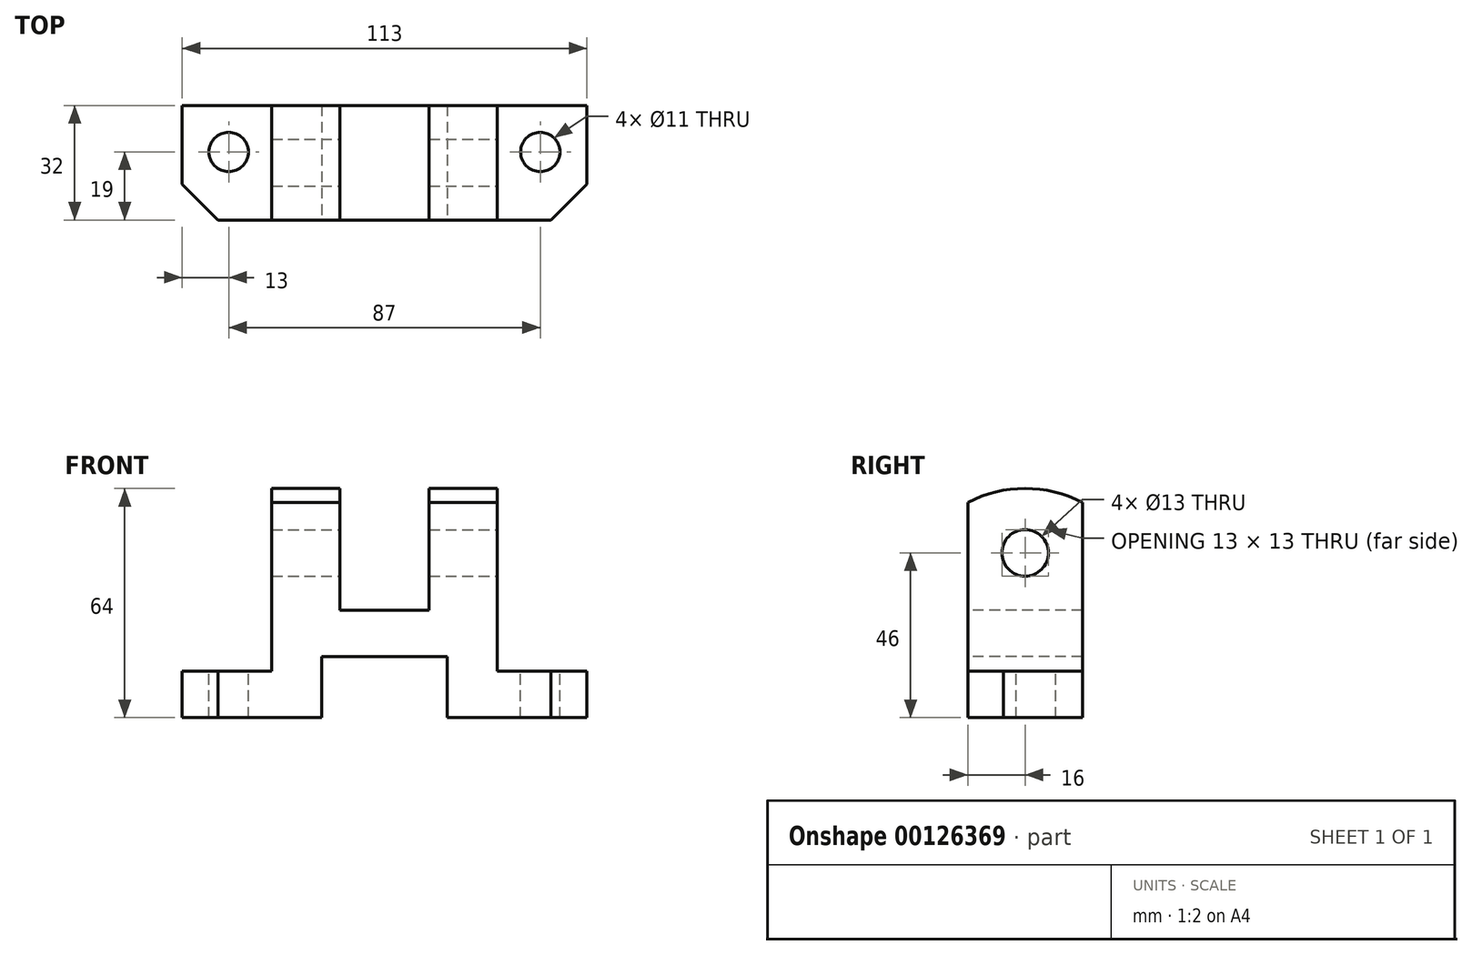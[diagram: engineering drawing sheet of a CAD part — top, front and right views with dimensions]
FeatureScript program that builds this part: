
annotation { "Feature Type Name" : "Feature", "Feature Type Description" : "" }
export const myFeature = defineFeature(function(context is Context, id is Id, definition is map)
    precondition{}
    {
        {
            var Q0;
            Q0=qCreatedBy(makeId("Front.planeOp"),FACE);
            var sketch = newSketch(context, id + "F0", { "sketchPlane" : qUnion([Q0])});
            skLineSegment(sketch, "E0", {"start": v(0, 0) * mm, "end": v(0, 13) * mm});
            skLineSegment(sketch, "E1", {"start": v(0, 13) * mm, "end": v(25, 13) * mm});
            skLineSegment(sketch, "E2", {"start": v(25, 13) * mm, "end": v(25, 64) * mm});
            skLineSegment(sketch, "E3", {"start": v(25, 64) * mm, "end": v(44, 64) * mm});
            skLineSegment(sketch, "E4", {"start": v(44, 64) * mm, "end": v(44, 30) * mm});
            skLineSegment(sketch, "E5", {"start": v(44, 30) * mm, "end": v(69, 30) * mm});
            skLineSegment(sketch, "E6", {"start": v(69, 30) * mm, "end": v(69, 64) * mm});
            skLineSegment(sketch, "E7", {"start": v(69, 64) * mm, "end": v(88, 64) * mm});
            skLineSegment(sketch, "E8", {"start": v(88, 64) * mm, "end": v(88, 13) * mm});
            skLineSegment(sketch, "E9", {"start": v(88, 13) * mm, "end": v(113, 13) * mm});
            skLineSegment(sketch, "E10", {"start": v(113, 13) * mm, "end": v(113, 0) * mm});
            skLineSegment(sketch, "E11", {"start": v(113, 0) * mm, "end": v(74, 0) * mm});
            skLineSegment(sketch, "E12", {"start": v(74, 0) * mm, "end": v(74, 17) * mm});
            skLineSegment(sketch, "E13", {"start": v(74, 17) * mm, "end": v(39, 17) * mm});
            skLineSegment(sketch, "E14", {"start": v(39, 17) * mm, "end": v(39, 0) * mm});
            skLineSegment(sketch, "E15", {"start": v(39, 0) * mm, "end": v(0, 0) * mm});
            skSolve(sketch);
        }
        {
            var Q0;
            Q0 = qSketchRegion(id + "F0", true);
            extrude(context, id + "F1", {"entities" : qUnion([Q0]), "oppositeDirection" : true, "depth" : 32 * mm});
        }
        {
            var Q0;
            Q0=makeQuery(id+"F1.opExtrude","SWEPT_FACE",FACE,{"disambiguationData":[OSD([sQuery(id+"F0.wireOp",EDGE,"E1")])]});
            var sketch = newSketch(context, id + "F2", { "sketchPlane" : qUnion([Q0])});
            skCircle(sketch, "E16", {"center": v(13, 19) * mm, "radius": 5.5 * mm});
            skSolve(sketch);
        }
        {
            var Q0;
            Q0 = qSketchRegion(id + "F2", true);
            extrude(context, id + "F3", {"entities" : qUnion([Q0]), "operationType" : NewBodyOperationType.REMOVE, "endBound" : BoundingType.THROUGH_ALL, "oppositeDirection" : true, "depth" : 25 * mm});
        }
        {
            var Q0;
            Q0=makeQuery(id+"F1.opExtrude","SWEPT_FACE",FACE,{"disambiguationData":[OSD([sQuery(id+"F0.wireOp",EDGE,"E9")])]});
            var sketch = newSketch(context, id + "F4", { "sketchPlane" : qUnion([Q0])});
            skCircle(sketch, "E17", {"center": v(100, 19) * mm, "radius": 5.5 * mm});
            skSolve(sketch);
        }
        {
            var Q0;
            Q0 = qSketchRegion(id + "F4", true);
            extrude(context, id + "F5", {"entities" : qUnion([Q0]), "operationType" : NewBodyOperationType.REMOVE, "endBound" : BoundingType.THROUGH_ALL, "oppositeDirection" : true, "depth" : 25 * mm});
        }
        {
            var Q0;
            Q0=makeQuery(id+"F1.opExtrude","SWEPT_FACE",FACE,{"disambiguationData":[OSD([sQuery(id+"F0.wireOp",EDGE,"E1")])]});
            var sketch = newSketch(context, id + "F6", { "sketchPlane" : qUnion([Q0])});
            skLineSegment(sketch, "E18", {"start": v(0, 0) * mm, "end": v(10, 0) * mm});
            skLineSegment(sketch, "E19", {"start": v(10, 0) * mm, "end": v(0, 10) * mm});
            skLineSegment(sketch, "E20", {"start": v(0, 10) * mm, "end": v(0, 0) * mm});
            skSolve(sketch);
        }
        {
            var Q0;
            Q0 = qSketchRegion(id + "F6", true);
            extrude(context, id + "F7", {"entities" : qUnion([Q0]), "operationType" : NewBodyOperationType.REMOVE, "endBound" : BoundingType.THROUGH_ALL, "oppositeDirection" : true, "depth" : 25 * mm});
        }
        {
            var Q0;
            Q0=makeQuery(id+"F1.opExtrude","SWEPT_FACE",FACE,{"disambiguationData":[OSD([sQuery(id+"F0.wireOp",EDGE,"E9")])]});
            var sketch = newSketch(context, id + "F8", { "sketchPlane" : qUnion([Q0])});
            skLineSegment(sketch, "E21", {"start": v(113, 0) * mm, "end": v(103, 0) * mm});
            skLineSegment(sketch, "E22", {"start": v(103, 0) * mm, "end": v(113, 10) * mm});
            skLineSegment(sketch, "E23", {"start": v(113, 10) * mm, "end": v(113, 0) * mm});
            skSolve(sketch);
        }
        {
            var Q0;
            Q0 = qSketchRegion(id + "F8", true);
            extrude(context, id + "F9", {"entities" : qUnion([Q0]), "operationType" : NewBodyOperationType.REMOVE, "endBound" : BoundingType.THROUGH_ALL, "oppositeDirection" : true, "depth" : 25 * mm});
        }
        {
            var Q0;
            Q0=makeQuery(id+"F1.opExtrude","SWEPT_FACE",FACE,{"disambiguationData":[OSD([sQuery(id+"F0.wireOp",EDGE,"E8")])]});
            var sketch = newSketch(context, id + "F10", { "sketchPlane" : qUnion([Q0])});
            skCircle(sketch, "E24", {"center": v(16, 46) * mm, "radius": 6.5 * mm});
            skSolve(sketch);
        }
        {
            var Q0;
            Q0 = qSketchRegion(id + "F10", true);
            extrude(context, id + "F11", {"entities" : qUnion([Q0]), "operationType" : NewBodyOperationType.REMOVE, "endBound" : BoundingType.THROUGH_ALL, "oppositeDirection" : true, "depth" : 25 * mm});
        }
        {
            var Q0;
            Q0=makeQuery(id+"F1.opExtrude","SWEPT_FACE",FACE,{"disambiguationData":[OSD([sQuery(id+"F0.wireOp",EDGE,"E8")])]});
            var sketch = newSketch(context, id + "F12", { "sketchPlane" : qUnion([Q0])});
            skArc(sketch, "E25", {"start": v(32, 60.13) * mm, "mid": v(16, 64) * mm, "end": v(0, 60.13) * mm});
            skLineSegment(sketch, "E26", {"start": v(0, 60.13) * mm, "end": v(0, 70.13) * mm});
            skLineSegment(sketch, "E27", {"start": v(0, 70.13) * mm, "end": v(32, 70.13) * mm});
            skLineSegment(sketch, "E28", {"start": v(32, 70.13) * mm, "end": v(32, 60.13) * mm});
            skSolve(sketch);
        }
        {
            var Q0;
            Q0 = qSketchRegion(id + "F12", true);
            extrude(context, id + "F13", {"entities" : qUnion([Q0]), "operationType" : NewBodyOperationType.REMOVE, "endBound" : BoundingType.THROUGH_ALL, "oppositeDirection" : true, "depth" : 25 * mm});
        }
    });
